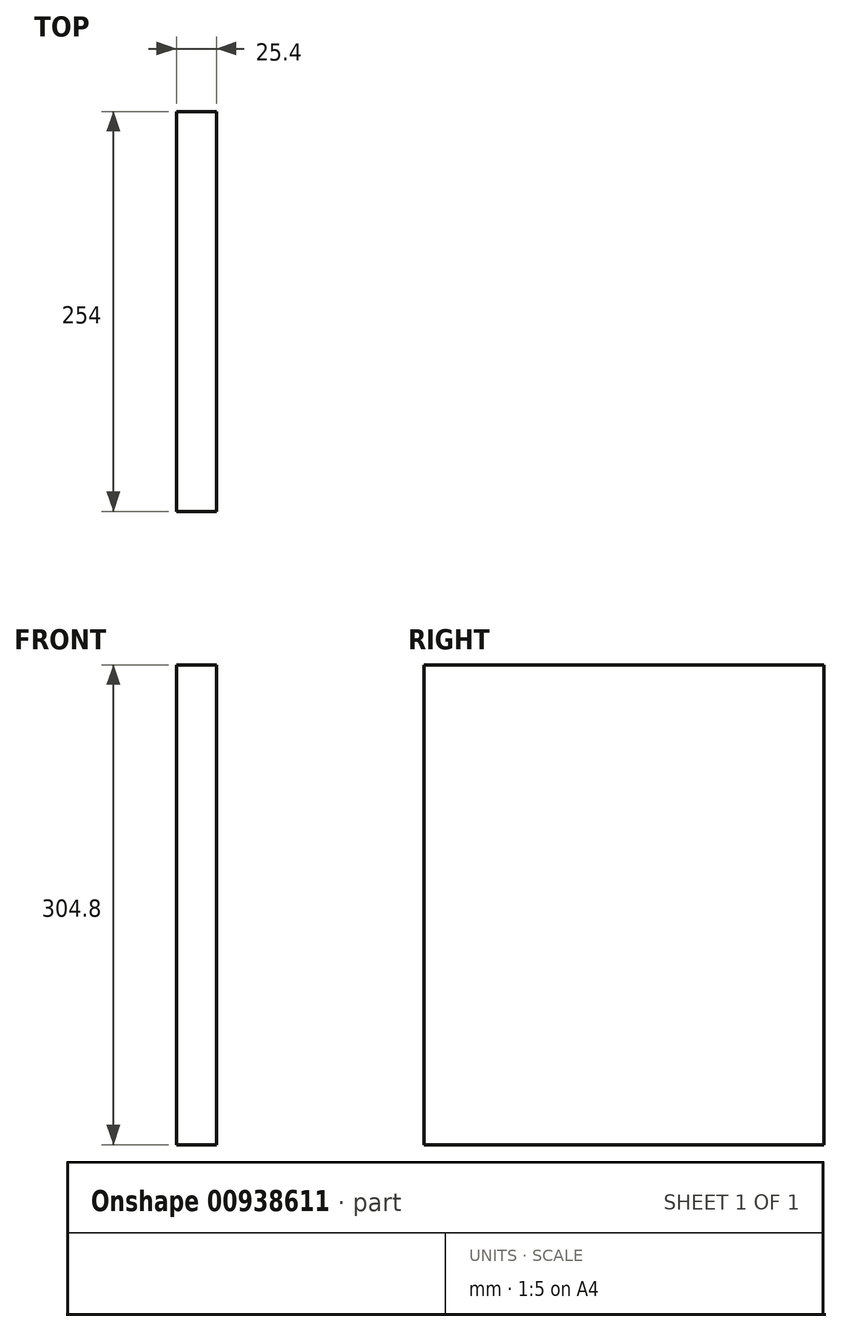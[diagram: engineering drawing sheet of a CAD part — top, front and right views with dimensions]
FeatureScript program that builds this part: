
annotation { "Feature Type Name" : "Feature", "Feature Type Description" : "" }
export const myFeature = defineFeature(function(context is Context, id is Id, definition is map)
    precondition{}
    {
        {
            var Q0;
            Q0=qCreatedBy(makeId("Right.planeOp"),FACE);
            var sketch = newSketch(context, id + "F0", { "sketchPlane" : qUnion([Q0])});
            skLineSegment(sketch, "E0.bottom", {"start": v(-127, 152.4) * mm, "end": v(127, 152.4) * mm});
            skLineSegment(sketch, "E0.top", {"start": v(-127, -152.4) * mm, "end": v(127, -152.4) * mm});
            skLineSegment(sketch, "E0.left", {"start": v(-127, 152.4) * mm, "end": v(-127, -152.4) * mm});
            skLineSegment(sketch, "E0.right", {"start": v(127, 152.4) * mm, "end": v(127, -152.4) * mm});
            skPoint(sketch, "E0.middle", {"position": v(0, 0) * mm});
            skSolve(sketch);
        }
        {
            var Q0;
            Q0=makeQuery(id+"F0.imprint","IMPRINT",FACE,{"disambiguationData":[TD([[makeQuery(id+"F0.imprint","IMPRINT",EDGE,{"derivedFrom":sQuery(id+"F0.wireOp",EDGE,"E0.bottom")}),-1.0]])]});
            extrude(context, id + "F1", {"entities" : qUnion([Q0]), "depth" : 25.4 * mm, "offsetDistance" : 25.4 * mm});
        }
    });
